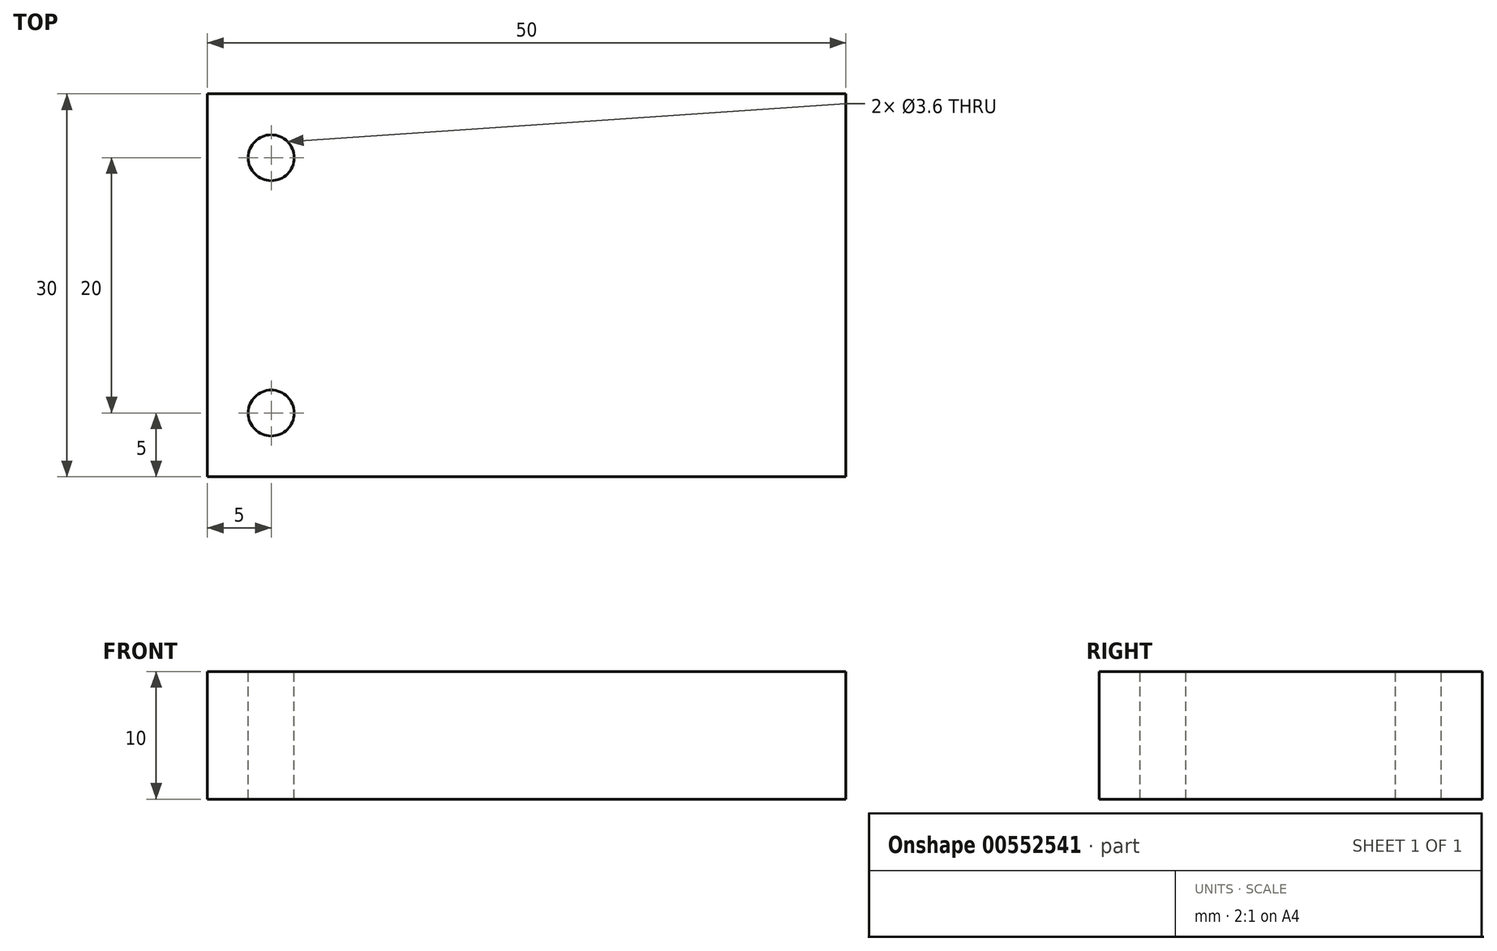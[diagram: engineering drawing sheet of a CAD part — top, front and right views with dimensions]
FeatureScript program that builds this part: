
annotation { "Feature Type Name" : "Feature", "Feature Type Description" : "" }
export const myFeature = defineFeature(function(context is Context, id is Id, definition is map)
    precondition{}
    {
        {
            var Q0;
            Q0=qCreatedBy(makeId("Top.planeOp"),FACE);
            var sketch = newSketch(context, id + "F0", { "sketchPlane" : qUnion([Q0])});
            skLineSegment(sketch, "E0.bottom", {"start": v(25, 15) * mm, "end": v(-25, 15) * mm});
            skLineSegment(sketch, "E0.top", {"start": v(25, -15) * mm, "end": v(-25, -15) * mm});
            skLineSegment(sketch, "E0.left", {"start": v(25, 15) * mm, "end": v(25, -15) * mm});
            skLineSegment(sketch, "E0.right", {"start": v(-25, 15) * mm, "end": v(-25, -15) * mm});
            skPoint(sketch, "E0.middle", {"position": v(0, 0) * mm});
            skSolve(sketch);
        }
        {
            var Q0;
            Q0 = qSketchRegion(id + "F0", true);
            extrude(context, id + "F1", {"entities" : qUnion([Q0]), "depth" : 10 * mm, "offsetDistance" : 25 * mm});
        }
        {
            var Q0;
            Q0=makeQuery(id+"F1.opExtrude","CAP_FACE",FACE,{"disambiguationData":[OSD([sQuery(id+"F0.wireOp",EDGE,"E0.bottom"),sQuery(id+"F0.wireOp",EDGE,"E0.top"),sQuery(id+"F0.wireOp",EDGE,"E0.left"),sQuery(id+"F0.wireOp",EDGE,"E0.right")])],"isStart":false});
            var sketch = newSketch(context, id + "F2", { "sketchPlane" : qUnion([Q0])});
            skCircle(sketch, "E1", {"center": v(-20, 10) * mm, "radius": 1.8 * mm});
            skCircle(sketch, "E2", {"center": v(-20, -10) * mm, "radius": 1.8 * mm});
            skSolve(sketch);
        }
        {
            var Q0;
            Q0 = qSketchRegion(id + "F2", true);
            extrude(context, id + "F3", {"entities" : qUnion([Q0]), "operationType" : NewBodyOperationType.REMOVE, "oppositeDirection" : true, "depth" : 15 * mm, "offsetDistance" : 25 * mm});
        }
    });
